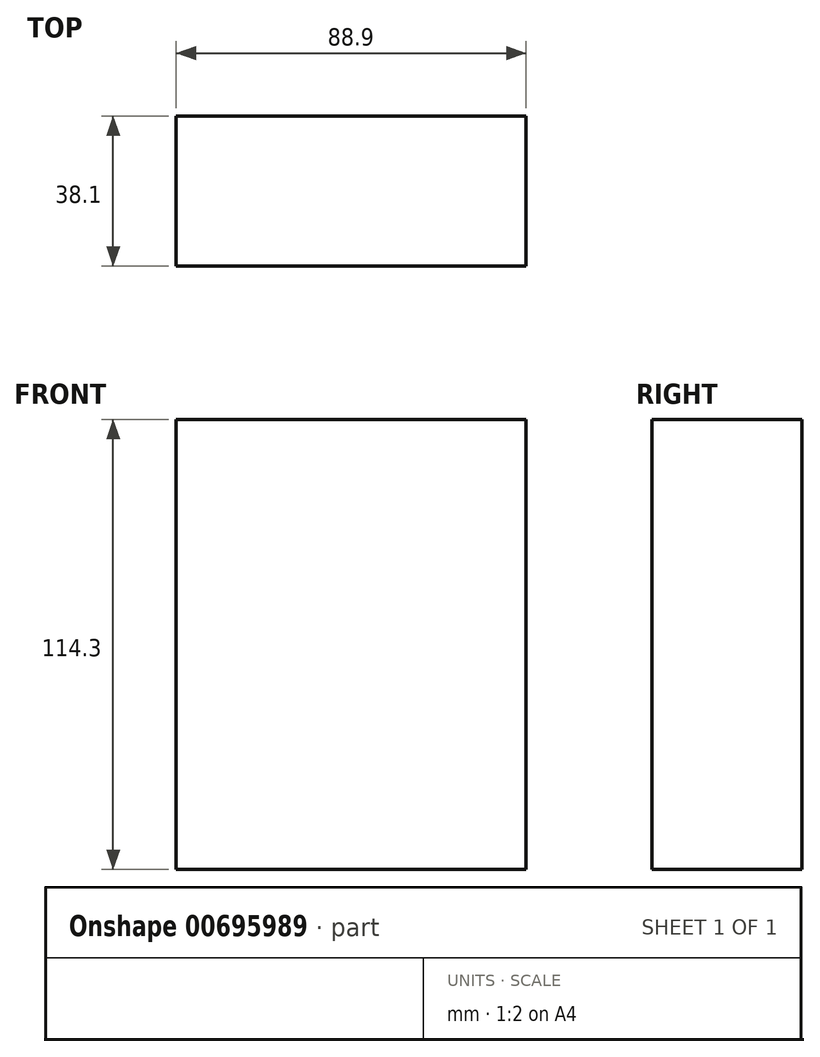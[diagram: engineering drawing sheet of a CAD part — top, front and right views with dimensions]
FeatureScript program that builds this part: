
annotation { "Feature Type Name" : "Feature", "Feature Type Description" : "" }
export const myFeature = defineFeature(function(context is Context, id is Id, definition is map)
    precondition{}
    {
        {
            var Q0;
            Q0=qCreatedBy(makeId("Front.planeOp"),FACE);
            var sketch = newSketch(context, id + "F0", { "sketchPlane" : qUnion([Q0])});
            skLineSegment(sketch, "E0.bottom", {"start": v(0, 0) * mm, "end": v(88.9, 0) * mm});
            skLineSegment(sketch, "E0.top", {"start": v(0, 114.3) * mm, "end": v(88.9, 114.3) * mm});
            skLineSegment(sketch, "E0.left", {"start": v(0, 0) * mm, "end": v(0, 114.3) * mm});
            skLineSegment(sketch, "E0.right", {"start": v(88.9, 0) * mm, "end": v(88.9, 114.3) * mm});
            skSolve(sketch);
        }
        {
            var Q0;
            Q0 = qSketchRegion(id + "F0", true);
            extrude(context, id + "F1", {"entities" : qUnion([Q0]), "depth" : 38.1 * mm, "offsetDistance" : 25.4 * mm});
        }
    });
